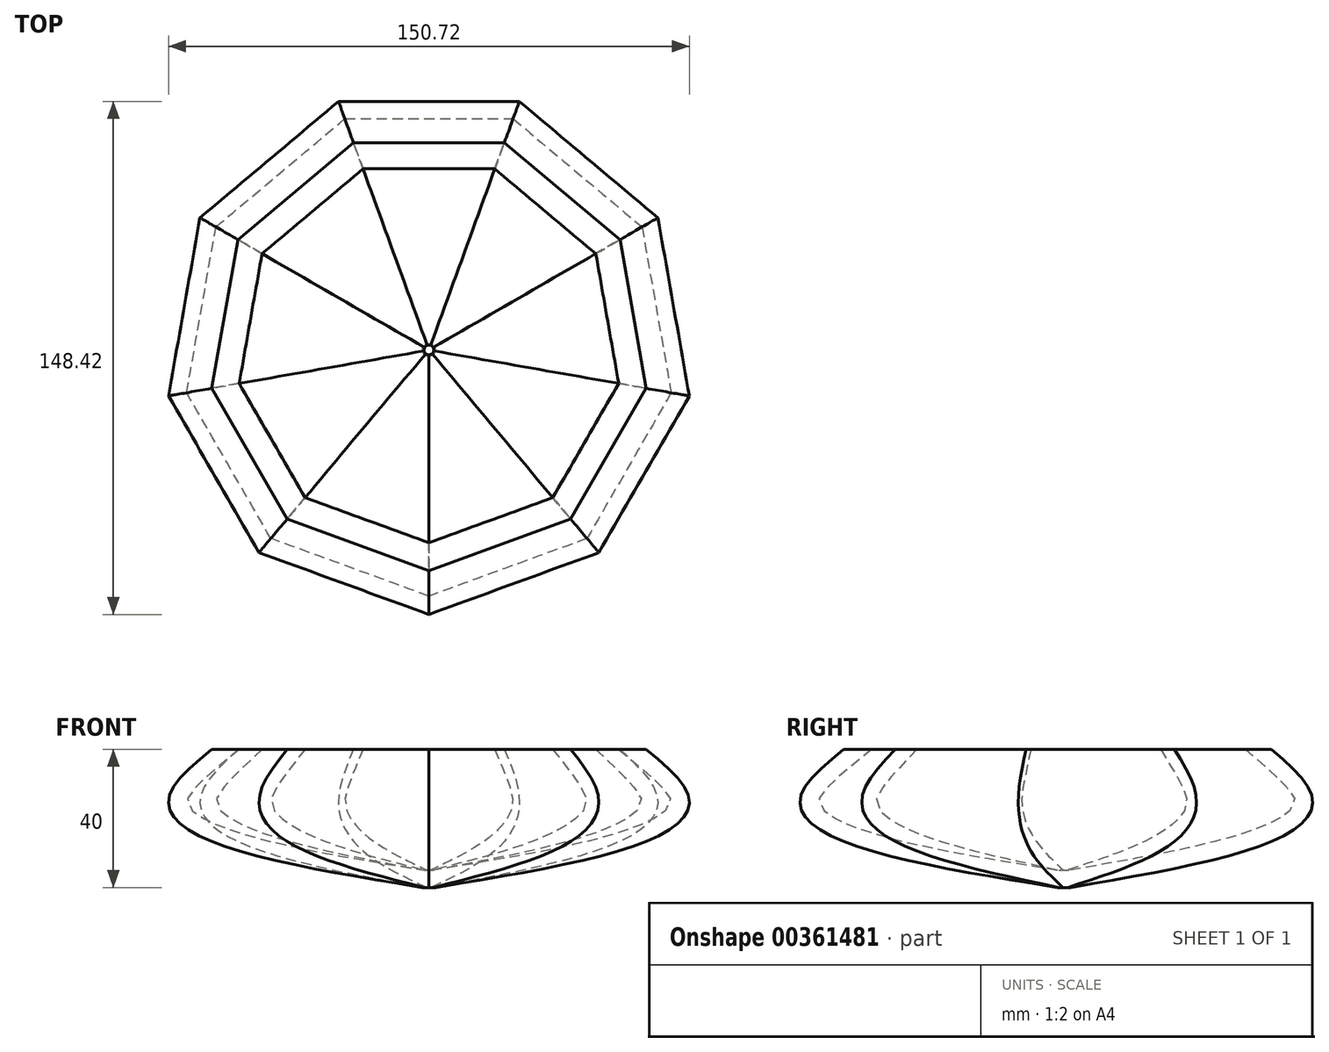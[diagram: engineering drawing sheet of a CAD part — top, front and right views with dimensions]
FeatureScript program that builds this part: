
annotation { "Feature Type Name" : "Feature", "Feature Type Description" : "" }
export const myFeature = defineFeature(function(context is Context, id is Id, definition is map)
    precondition{}
    {
        {
            var Q0;
            Q0=qCreatedBy(makeId("Top.planeOp"),FACE);
            var sketch = newSketch(context, id + "F0", { "sketchPlane" : qUnion([Q0])});
            skCircle(sketch, "E0.cCircle", {"center": v(0, 0) * mm, "radius": 70 * mm, "construction": true});
            skLineSegment(sketch, "E0.0", {"start": v(-25.48, 70) * mm, "end": v(25.48, 70) * mm});
            skLineSegment(sketch, "E0.1", {"start": v(25.48, 70) * mm, "end": v(64.51, 37.25) * mm});
            skLineSegment(sketch, "E0.2", {"start": v(64.51, 37.25) * mm, "end": v(73.36, -12.94) * mm});
            skLineSegment(sketch, "E0.3", {"start": v(73.36, -12.94) * mm, "end": v(47.88, -57.06) * mm});
            skLineSegment(sketch, "E0.4", {"start": v(47.88, -57.06) * mm, "end": v(0, -74.5) * mm});
            skLineSegment(sketch, "E0.5", {"start": v(0, -74.5) * mm, "end": v(-47.88, -57.06) * mm});
            skLineSegment(sketch, "E0.6", {"start": v(-47.88, -57.06) * mm, "end": v(-73.36, -12.94) * mm});
            skLineSegment(sketch, "E0.7", {"start": v(-73.36, -12.94) * mm, "end": v(-64.51, 37.25) * mm});
            skLineSegment(sketch, "E0.8", {"start": v(-64.51, 37.25) * mm, "end": v(-25.48, 70) * mm});
            skPoint(sketch, "E0.0.midPoint", {"position": v(0, 70) * mm});
            skSolve(sketch);
        }
        {
            var Q0;
            Q0=qCreatedBy(makeId("Top.planeOp"),FACE);
            cPlane(context, id + "F1", {"entities" : qUnion([Q0]), "cplaneType" : CPlaneType.OFFSET, "offset" : 10 * mm, "width" : 152.4 * mm, "height" : 152.4 * mm});
        }
        {
            var Q0;
            Q0=qCreatedBy(id+"F1.planeOp",FACE);
            var sketch = newSketch(context, id + "F2", { "sketchPlane" : qUnion([Q0])});
            skCircle(sketch, "E1.cCircle", {"center": v(0, 0) * mm, "radius": 60 * mm, "construction": true});
            skLineSegment(sketch, "E1.0", {"start": v(-21.84, 60) * mm, "end": v(21.84, 60) * mm});
            skLineSegment(sketch, "E1.1", {"start": v(21.84, 60) * mm, "end": v(55.3, 31.93) * mm});
            skLineSegment(sketch, "E1.2", {"start": v(55.3, 31.93) * mm, "end": v(62.88, -11.09) * mm});
            skLineSegment(sketch, "E1.3", {"start": v(62.88, -11.09) * mm, "end": v(41.04, -48.91) * mm});
            skLineSegment(sketch, "E1.4", {"start": v(41.04, -48.91) * mm, "end": v(0, -63.85) * mm});
            skLineSegment(sketch, "E1.5", {"start": v(0, -63.85) * mm, "end": v(-41.04, -48.91) * mm});
            skLineSegment(sketch, "E1.6", {"start": v(-41.04, -48.91) * mm, "end": v(-62.88, -11.09) * mm});
            skLineSegment(sketch, "E1.7", {"start": v(-62.88, -11.09) * mm, "end": v(-55.3, 31.93) * mm});
            skLineSegment(sketch, "E1.8", {"start": v(-55.3, 31.93) * mm, "end": v(-21.84, 60) * mm});
            skPoint(sketch, "E1.0.midPoint", {"position": v(0, 60) * mm});
            skSolve(sketch);
        }
        {
            var Q0;
            Q0=qCreatedBy(makeId("Top.planeOp"),FACE);
            cPlane(context, id + "F3", {"entities" : qUnion([Q0]), "cplaneType" : CPlaneType.OFFSET, "offset" : 30 * mm, "oppositeDirection" : true, "width" : 152.4 * mm, "height" : 152.4 * mm});
        }
        {
            var Q0;
            Q0=qCreatedBy(id+"F3.planeOp",FACE);
            var sketch = newSketch(context, id + "F4", { "sketchPlane" : qUnion([Q0])});
            skCircle(sketch, "E2.cCircle", {"center": v(0, 0) * mm, "radius": 1.81 * mm, "construction": true});
            skLineSegment(sketch, "E2.0", {"start": v(-0.66, 1.81) * mm, "end": v(0.66, 1.81) * mm});
            skLineSegment(sketch, "E2.1", {"start": v(0.66, 1.81) * mm, "end": v(1.67, 0.96) * mm});
            skLineSegment(sketch, "E2.2", {"start": v(1.67, 0.96) * mm, "end": v(1.9, -0.34) * mm});
            skLineSegment(sketch, "E2.3", {"start": v(1.9, -0.34) * mm, "end": v(1.24, -1.48) * mm});
            skLineSegment(sketch, "E2.4", {"start": v(1.24, -1.48) * mm, "end": v(0, -1.93) * mm});
            skLineSegment(sketch, "E2.5", {"start": v(0, -1.93) * mm, "end": v(-1.24, -1.48) * mm});
            skLineSegment(sketch, "E2.6", {"start": v(-1.24, -1.48) * mm, "end": v(-1.9, -0.34) * mm});
            skLineSegment(sketch, "E2.7", {"start": v(-1.9, -0.34) * mm, "end": v(-1.67, 0.96) * mm});
            skLineSegment(sketch, "E2.8", {"start": v(-1.67, 0.96) * mm, "end": v(-0.66, 1.81) * mm});
            skPoint(sketch, "E2.0.midPoint", {"position": v(0, 1.81) * mm});
            skSolve(sketch);
        }
        {
            var Q0;
            Q0=makeQuery(id+"F2.imprint","IMPRINT",FACE,{"disambiguationData":[TD([[makeQuery(id+"F2.imprint","IMPRINT",EDGE,{"derivedFrom":sQuery(id+"F2.wireOp",EDGE,"E1.0")}),-1.0]])]});
            var Q1;
            Q1=makeQuery(id+"F0.imprint","IMPRINT",FACE,{"disambiguationData":[TD([[makeQuery(id+"F0.imprint","IMPRINT",EDGE,{"derivedFrom":sQuery(id+"F0.wireOp",EDGE,"E0.0")}),-1.0]])]});
            var Q2;
            Q2=makeQuery(id+"F4.imprint","IMPRINT",FACE,{"disambiguationData":[TD([[makeQuery(id+"F4.imprint","IMPRINT",EDGE,{"derivedFrom":sQuery(id+"F4.wireOp",EDGE,"E2.0")}),-1.0]])]});
            loft(context, id + "F5", {"sheetProfilesArray" : [{ "sheetProfileEntities" : qUnion([Q0]) }, { "sheetProfileEntities" : qUnion([Q1]) }, { "sheetProfileEntities" : qUnion([Q2]) }]});
        }
        {
            var Q0;
            Q0=makeQuery(id+"F5.opLoft","CAP_FACE",FACE,{"disambiguationData":[OSD([makeQuery(id+"F2.imprint","IMPRINT",FACE,{"disambiguationData":[TD([[makeQuery(id+"F2.imprint","IMPRINT",EDGE,{"derivedFrom":sQuery(id+"F2.wireOp",EDGE,"E1.0")}),-1.0]])]})])],"isStart":true});
            shell(context, id + "F6", {"entities" : qUnion([Q0]), "thickness" : 5 * mm});
        }
    });
